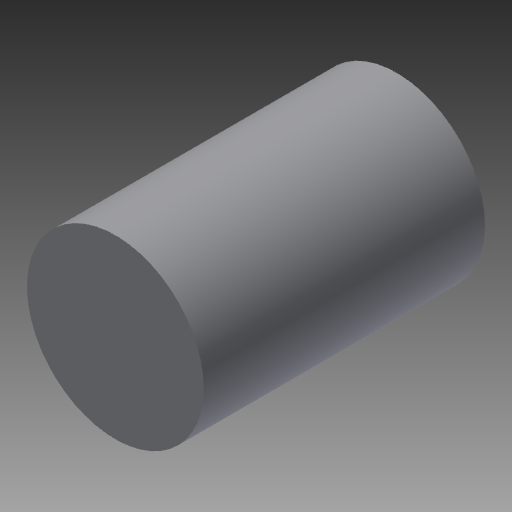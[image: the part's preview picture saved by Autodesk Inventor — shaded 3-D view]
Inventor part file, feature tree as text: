
AUTODESK INVENTOR PART (.ipt)
format: ipt  version: 2017.1 (Build 211199000, 199)  size: 99,328 bytes
history: native  units: in
note: dims shown in document units (in); Inventor stores cm internally (conversion verified against a paired STEP export)
features: plane x1, extrude x1, sketch x1, reference x1
ambient origin geometry x8: Origin, YZ Plane, XZ Plane, XY Plane, X Axis, Y Axis, Z Axis, Center Point
bodies: Solid1 (feature_tree)
feature tree (4):
  plane  "Work Plane1"
  extrude  "Extrusion1"  Depth=3.358in TaperAngle=0.0deg
  sketch  "Sketch1"  dims[d0=2.11in d1=3.358in d2=0.0in]
  reference  "Reference1"
